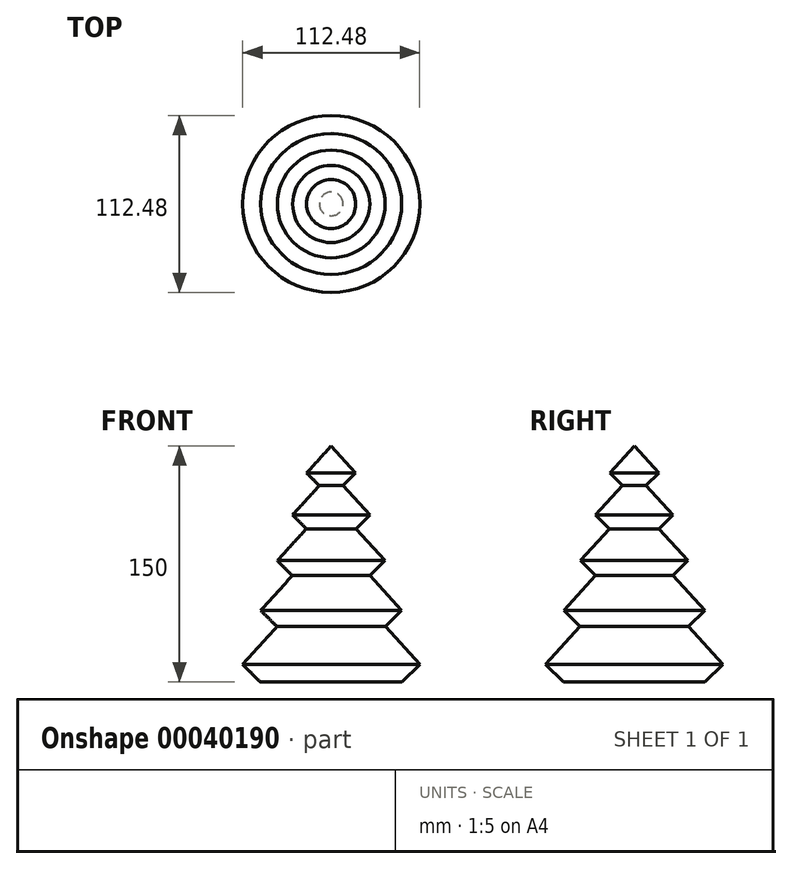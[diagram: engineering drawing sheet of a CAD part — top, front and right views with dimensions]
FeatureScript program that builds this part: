
annotation { "Feature Type Name" : "Feature", "Feature Type Description" : "" }
export const myFeature = defineFeature(function(context is Context, id is Id, definition is map)
    precondition{}
    {
        {
            var Q0;
            Q0=qCreatedBy(makeId("Front.planeOp"),FACE);
            var sketch = newSketch(context, id + "F0", { "sketchPlane" : qUnion([Q0])});
            skLineSegment(sketch, "E0", {"start": v(0, 0) * mm, "end": v(0, 179.48) * mm});
            skLineSegment(sketch, "E1", {"start": v(0, 179.48) * mm, "end": v(60, 0) * mm, "construction": true});
            skLineSegment(sketch, "E2", {"start": v(60, 0) * mm, "end": v(0, 0) * mm});
            skLineSegment(sketch, "E3", {"start": v(45, 0) * mm, "end": v(56.24, 11.24) * mm});
            skLineSegment(sketch, "E4", {"start": v(34.43, 35.24) * mm, "end": v(44.76, 45.58) * mm});
            skLineSegment(sketch, "E5", {"start": v(34.43, 35.24) * mm, "end": v(56.24, 11.24) * mm});
            skLineSegment(sketch, "E6", {"start": v(24.7, 67.64) * mm, "end": v(44.76, 45.58) * mm});
            skLineSegment(sketch, "E7", {"start": v(24.7, 67.64) * mm, "end": v(34.21, 77.14) * mm});
            skLineSegment(sketch, "E8", {"start": v(34.21, 77.14) * mm, "end": v(15.77, 97.43) * mm});
            skLineSegment(sketch, "E9", {"start": v(15.77, 97.43) * mm, "end": v(24.5, 106.17) * mm});
            skLineSegment(sketch, "E10", {"start": v(24.5, 106.17) * mm, "end": v(7.55, 124.82) * mm});
            skLineSegment(sketch, "E11", {"start": v(7.55, 124.82) * mm, "end": v(15.59, 132.85) * mm});
            skLineSegment(sketch, "E12", {"start": v(15.59, 132.85) * mm, "end": v(0, 150) * mm});
            skLineSegment(sketch, "E13", {"start": v(0, 150) * mm, "end": v(45, 0) * mm, "construction": true});
            skSolve(sketch);
        }
        {
            var Q0;
            {var subQ2=sQuery(id+"F0.wireOp",EDGE,"E0");Q0=makeQuery(id+"F0.imprint","IMPRINT",FACE,{"disambiguationData":[TD([[makeQuery(id+"F0.imprint","IMPRINT",EDGE,{"derivedFrom":subQ2}),-1.0]])]});}
            var Q1;
            Q1=sQuery(id+"F0.wireOp",EDGE,"E0");
            revolve(context, id + "F1", {"entities" : qUnion([Q0]), "axis" : qUnion([Q1]), "revolveType" : RevolveType.FULL});
        }
    });
